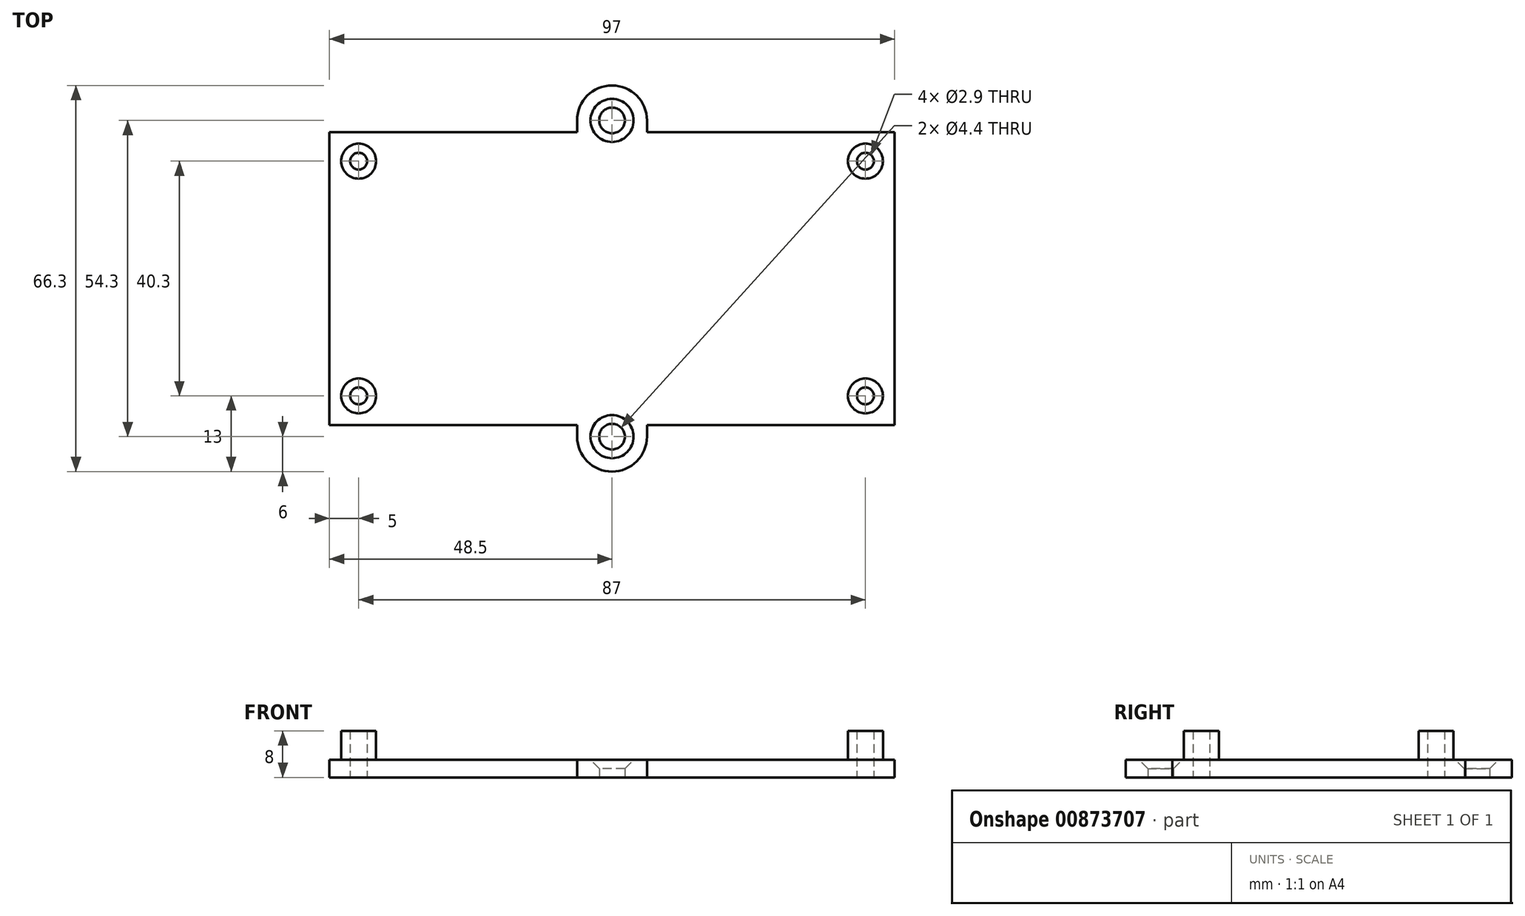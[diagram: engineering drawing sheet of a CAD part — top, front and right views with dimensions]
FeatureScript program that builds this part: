
annotation { "Feature Type Name" : "Feature", "Feature Type Description" : "" }
export const myFeature = defineFeature(function(context is Context, id is Id, definition is map)
    precondition{}
    {
        {
            var Q0;
            Q0=qCreatedBy(makeId("Top.planeOp"),FACE);
            var sketch = newSketch(context, id + "F0", { "sketchPlane" : qUnion([Q0])});
            skLineSegment(sketch, "E0.bottom", {"start": v(43.5, -20.15) * mm, "end": v(-43.5, -20.15) * mm, "construction": true});
            skLineSegment(sketch, "E0.top", {"start": v(43.5, 20.15) * mm, "end": v(-43.5, 20.15) * mm, "construction": true});
            skLineSegment(sketch, "E0.left", {"start": v(43.5, -20.15) * mm, "end": v(43.5, 20.15) * mm, "construction": true});
            skLineSegment(sketch, "E0.right", {"start": v(-43.5, -20.15) * mm, "end": v(-43.5, 20.15) * mm, "construction": true});
            skPoint(sketch, "E0.middle", {"position": v(0, 0) * mm});
            skCircle(sketch, "E1", {"center": v(-43.5, 20.15) * mm, "radius": 3 * mm});
            skCircle(sketch, "E2", {"center": v(43.5, 20.15) * mm, "radius": 3 * mm});
            skCircle(sketch, "E3", {"center": v(-43.5, -20.15) * mm, "radius": 3 * mm});
            skCircle(sketch, "E4", {"center": v(43.5, -20.15) * mm, "radius": 3 * mm});
            skCircle(sketch, "E5", {"center": v(-43.5, 20.15) * mm, "radius": 1.45 * mm});
            skCircle(sketch, "E6", {"center": v(43.5, 20.15) * mm, "radius": 1.45 * mm});
            skCircle(sketch, "E7", {"center": v(43.5, -20.15) * mm, "radius": 1.45 * mm});
            skCircle(sketch, "E8", {"center": v(-43.5, -20.15) * mm, "radius": 1.45 * mm});
            skLineSegment(sketch, "E9.0", {"start": v(48.5, 25.15) * mm, "end": v(4.58, 25.15) * mm});
            skLineSegment(sketch, "E9.1", {"start": v(48.5, -25.15) * mm, "end": v(48.5, 25.15) * mm});
            skLineSegment(sketch, "E9.2", {"start": v(48.5, -25.15) * mm, "end": v(6, -25.15) * mm});
            skLineSegment(sketch, "E9.3", {"start": v(-48.5, -25.15) * mm, "end": v(-48.5, 25.15) * mm});
            skCircle(sketch, "E10", {"center": v(0, 27.15) * mm, "radius": 2.2 * mm});
            skArc(sketch, "E11", {"start": v(6, 27.15) * mm, "mid": v(0, 33.15) * mm, "end": v(-6, 27.15) * mm});
            skLineSegment(sketch, "E12", {"start": v(6, 25.15) * mm, "end": v(6, 27.15) * mm});
            skLineSegment(sketch, "E13", {"start": v(-6, 27.15) * mm, "end": v(-6, 25.15) * mm});
            skLineSegment(sketch, "E14.trimOffspring", {"start": v(-4.58, 25.15) * mm, "end": v(-48.5, 25.15) * mm});
            skCircle(sketch, "E15.MirrorC", {"center": v(0, -27.15) * mm, "radius": 2.2 * mm});
            skArc(sketch, "E16.MirrorCS", {"start": v(6, -27.15) * mm, "mid": v(0, -33.15) * mm, "end": v(-6, -27.15) * mm});
            skLineSegment(sketch, "E17.MirrorCS", {"start": v(-6, -27.15) * mm, "end": v(-6, -25.15) * mm});
            skLineSegment(sketch, "E18.MirrorCS", {"start": v(6, -25.15) * mm, "end": v(6, -27.15) * mm});
            skLineSegment(sketch, "E19.trimOffspring", {"start": v(-6, -25.15) * mm, "end": v(-48.5, -25.15) * mm});
            skSolve(sketch);
        }
        {
            var Q0;
            Q0=makeQuery(id+"F0.imprint","IMPRINT",FACE,{"disambiguationData":[TD([[makeQuery(id+"F0.imprint","IMPRINT",EDGE,{"derivedFrom":sQuery(id+"F0.wireOp",EDGE,"E1")}),-1.0]])]});
            var Q1;
            Q1=makeQuery(id+"F0.imprint","IMPRINT",FACE,{"disambiguationData":[TD([[makeQuery(id+"F0.imprint","IMPRINT",EDGE,{"derivedFrom":sQuery(id+"F0.wireOp",EDGE,"E1")}),1.0]])]});
            var Q2;
            Q2=makeQuery(id+"F0.imprint","IMPRINT",FACE,{"disambiguationData":[TD([[makeQuery(id+"F0.imprint","IMPRINT",EDGE,{"derivedFrom":sQuery(id+"F0.wireOp",EDGE,"E3")}),1.0]])]});
            var Q3;
            Q3=makeQuery(id+"F0.imprint","IMPRINT",FACE,{"disambiguationData":[TD([[makeQuery(id+"F0.imprint","IMPRINT",EDGE,{"derivedFrom":sQuery(id+"F0.wireOp",EDGE,"E4")}),1.0]])]});
            var Q4;
            Q4=makeQuery(id+"F0.imprint","IMPRINT",FACE,{"disambiguationData":[TD([[makeQuery(id+"F0.imprint","IMPRINT",EDGE,{"derivedFrom":sQuery(id+"F0.wireOp",EDGE,"E2")}),1.0]])]});
            extrude(context, id + "F1", {"entities" : qUnion([Q0, Q1, Q2, Q3, Q4]), "depth" : 3 * mm, "offsetDistance" : 25 * mm});
        }
        {
            var Q0;
            Q0=makeQuery(id+"F0.imprint","IMPRINT",FACE,{"disambiguationData":[TD([[makeQuery(id+"F0.imprint","IMPRINT",EDGE,{"derivedFrom":sQuery(id+"F0.wireOp",EDGE,"E1")}),1.0]])]});
            var Q1;
            Q1=makeQuery(id+"F0.imprint","IMPRINT",FACE,{"disambiguationData":[TD([[makeQuery(id+"F0.imprint","IMPRINT",EDGE,{"derivedFrom":sQuery(id+"F0.wireOp",EDGE,"E3")}),1.0]])]});
            var Q2;
            Q2=makeQuery(id+"F0.imprint","IMPRINT",FACE,{"disambiguationData":[TD([[makeQuery(id+"F0.imprint","IMPRINT",EDGE,{"derivedFrom":sQuery(id+"F0.wireOp",EDGE,"E2")}),1.0]])]});
            var Q3;
            Q3=makeQuery(id+"F0.imprint","IMPRINT",FACE,{"disambiguationData":[TD([[makeQuery(id+"F0.imprint","IMPRINT",EDGE,{"derivedFrom":sQuery(id+"F0.wireOp",EDGE,"E4")}),1.0]])]});
            extrude(context, id + "F2", {"entities" : qUnion([Q0, Q1, Q2, Q3]), "operationType" : NewBodyOperationType.ADD, "depth" : 8 * mm, "offsetDistance" : 25 * mm});
        }
        {
            var Q0;
            Q0=makeQuery(id+"F1.opExtrude","CAP_EDGE",EDGE,{"disambiguationData":[OSD([sQuery(id+"F0.wireOp",EDGE,"E10")])],"isStart":false});
            var Q1;
            Q1=makeQuery(id+"F1.opExtrude","CAP_EDGE",EDGE,{"disambiguationData":[OSD([sQuery(id+"F0.wireOp",EDGE,"E15.MirrorC")])],"isStart":false});
            chamfer(context, id + "F3", {"entities" : qUnion([Q0, Q1]), "width" : 1.5 * mm, "tangentPropagation" : true});
        }
    });
